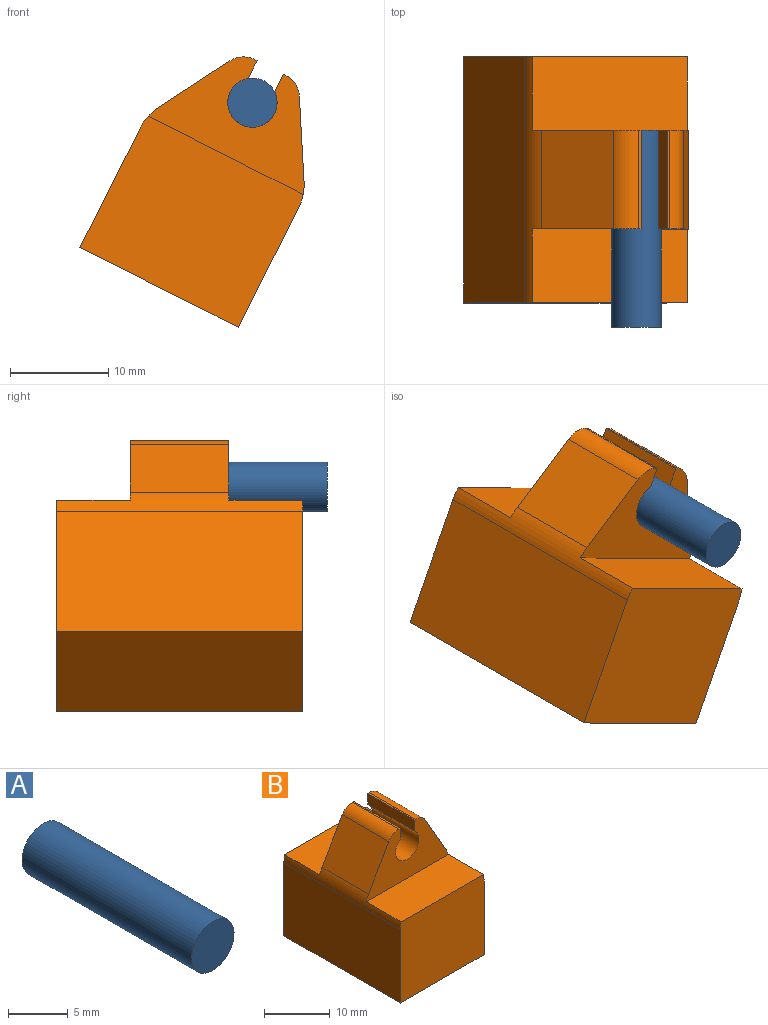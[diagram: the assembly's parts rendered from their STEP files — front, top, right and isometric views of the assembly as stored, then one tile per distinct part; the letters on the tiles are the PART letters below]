
ASSEMBLY  parts=2 mates=1
PART A: 3 faces, bbox 5x20x5 mm
  f0: cylinder r=2.5mm len=20mm, axis (0,1,0), area 314.2mm2, adj f1,f2
  f1: plane 5x5mm, normal (0,-1,0), area 19.6mm2, adj f0
  f2: plane 5x5mm, normal (0,1,0), area 19.6mm2, adj f0
PART B: 20 faces, bbox 18x25x25 mm
  f0: plane 17.63x7.5mm, normal (0,0,1), area 132.3mm2, adj f2,f13,f18,f19
  f1: plane 25x13.66mm, normal (-1,0,0), area 341.5mm2, adj f2,f4,f6,f18
  f2: plane 18x15mm, normal (0,-1,0), area 269.8mm2, adj f0,f1,f3,f6,f18,f19
  f3: plane 25x13.66mm, normal (1,0,0), area 341.5mm2, adj f2,f4,f6,f19
  f4: plane 18x15mm, normal (0,1,0), area 269.8mm2, adj f1,f3,f5,f6,f18,f19
  f5: plane 17.63x7.5mm, normal (0,0,1), area 132.3mm2, adj f4,f14,f18,f19
  f6: plane 25x18mm, normal (0,0,-1), area 450mm2, adj f1,f2,f3,f4
  f7: plane 10x7.59mm, normal (-0.87,0,0.5), area 87.6mm2, adj f13,f14,f17,f18
  f8: plane 10x7.59mm, normal (0.87,0,0.5), area 87.6mm2, adj f13,f14,f16,f19
  f9: plane 10x0.28mm, normal (0,0,1), area 2.8mm2, adj f10,f13,f14,f16
  f10: plane 10x2mm, normal (-1,0,0), area 20mm2, adj f9,f13,f14,f15
  f11: plane 10x2mm, normal (1,0,0), area 20mm2, adj f12,f13,f14,f15
  f12: plane 10x0.28mm, normal (0,0,1), area 2.8mm2, adj f11,f13,f14,f17
  f13: plane 17.63x10mm, normal (0,-1,0), area 96.8mm2, adj f0,f7,f8,f9,f10,f11,f12,f15
  f14: plane 17.63x10mm, normal (0,1,0), area 96.8mm2, adj f5,f7,f8,f9,f10,f11,f12,f15
  f15: cylinder r=2.5mm len=10mm, axis (0,-1,0), area 124.9mm2, adj f10,f11,f13,f14
  f16: cylinder r=2.5mm len=10mm, axis (0,1,0), area 26.2mm2, adj f8,f9,f13,f14
  f17: cylinder r=2.5mm len=10mm, axis (0,1,0), area 26.2mm2, adj f7,f12,f13,f14
  f18: cylinder r=5mm len=25mm, axis (0,1,0), area 46.5mm2, adj f0,f1,f2,f4,f5,f7,f13,f14
  f19: cylinder r=5mm len=25mm, axis (0,-1,0), area 46.5mm2, adj f0,f2,f3,f4,f5,f8,f13,f14
PLACE A at identity fixed
PLACE B rot(axis=(0,1,0),26.9deg) t=(-17.52,-17.5,-14.67)mm
MATE revolute B.f15 <-> A.f0  axis (0,-1,0) through (0,-10,0)mm
